annotation { "Feature Type Name" : "Feature", "Feature Type Description" : "" }
export const myFeature = defineFeature(function(context is Context, id is Id, definition is map)
    precondition{}
    {
        {
            var Q0;
            Q0=qCreatedBy(makeId("Front.planeOp"),FACE);
            var sketch = newSketch(context, id + "F0", { "sketchPlane" : qUnion([Q0])});
            skLineSegment(sketch, "E0.bottom", {"start": v(-23.42, 52.83) * mm, "end": v(52.78, 52.83) * mm});
            skLineSegment(sketch, "E0.top", {"start": v(-23.42, -61.47) * mm, "end": v(52.78, -61.47) * mm});
            skLineSegment(sketch, "E0.left", {"start": v(-23.42, 52.83) * mm, "end": v(-23.42, -61.47) * mm});
            skLineSegment(sketch, "E0.right", {"start": v(52.78, 52.83) * mm, "end": v(52.78, -61.47) * mm});
            skSolve(sketch);
        }
        {
            var Q0;
            Q0 = qSketchRegion(id + "F0", true);
            extrude(context, id + "F1", {"entities" : qUnion([Q0]), "depth" : 3.17 * mm});
        }
        {
            var Q0;
            Q0=makeQuery(id+"F1.opExtrude","CAP_FACE",FACE,{"disambiguationData":[OSD([sQuery(id+"F0.wireOp",EDGE,"E0.bottom"),sQuery(id+"F0.wireOp",EDGE,"E0.top"),sQuery(id+"F0.wireOp",EDGE,"E0.left"),sQuery(id+"F0.wireOp",EDGE,"E0.right")])],"isStart":false});
            var sketch = newSketch(context, id + "F2", { "sketchPlane" : qUnion([Q0])});
            skText(sketch, "E1", { "text": "STEM Academy\n", "fontName": "OpenSans-Regular.ttf"});
            const initialGuessF2  = {"E1": [-0.02342, 0.0339, 1, 0, 0.00766]};
            skSetInitialGuess(sketch, initialGuessF2);
            skSolve(sketch);
        }
        {
            var Q0;
            Q0 = qSketchRegion(id + "F2", true);
            extrude(context, id + "F3", {"entities" : qUnion([Q0]), "operationType" : NewBodyOperationType.REMOVE, "oppositeDirection" : true, "depth" : 3.17 * mm});
        }
        {
            var Q0;
            {var subQ0=sQuery(id+"F0.wireOp",EDGE,"E0.top");var subQ1=sQuery(id+"F0.wireOp",EDGE,"E0.right");var subQ2=sQuery(id+"F0.wireOp",EDGE,"E0.bottom");var subQ3=sQuery(id+"F0.wireOp",EDGE,"E0.left");Q0=makeQuery(id+"F3.boolean.opBoolean","SPLIT",FACE,{"disambiguationData":[TD([makeQuery(id+"F1.opExtrude","SWEPT_FACE",FACE,{"disambiguationData":[OSD([subQ2])]})])],"derivedFrom":makeQuery(id+"F1.opExtrude","CAP_FACE",FACE,{"disambiguationData":[OSD([subQ2,subQ0,subQ3,subQ1])],"isStart":false})});}
            var sketch = newSketch(context, id + "F4", { "sketchPlane" : qUnion([Q0])});
            skCircle(sketch, "E2", {"center": v(12.38, 47.2) * mm, "radius": 3.66 * mm});
            skSolve(sketch);
        }
        {
            var Q0;
            Q0 = qSketchRegion(id + "F4", true);
            extrude(context, id + "F5", {"entities" : qUnion([Q0]), "operationType" : NewBodyOperationType.REMOVE, "oppositeDirection" : true, "depth" : 25.4 * mm});
        }
        {
            var Q0;
            {var subQ0=sQuery(id+"F0.wireOp",EDGE,"E0.top");var subQ1=sQuery(id+"F0.wireOp",EDGE,"E0.right");var subQ2=sQuery(id+"F0.wireOp",EDGE,"E0.bottom");var subQ3=sQuery(id+"F0.wireOp",EDGE,"E0.left");Q0=makeQuery(id+"F3.boolean.opBoolean","SPLIT",FACE,{"disambiguationData":[TD([makeQuery(id+"F1.opExtrude","SWEPT_FACE",FACE,{"disambiguationData":[OSD([subQ2])]})])],"derivedFrom":makeQuery(id+"F1.opExtrude","CAP_FACE",FACE,{"disambiguationData":[OSD([subQ2,subQ0,subQ3,subQ1])],"isStart":false})});}
            var sketch = newSketch(context, id + "F6", { "sketchPlane" : qUnion([Q0])});
            skLineSegment(sketch, "E3", {"start": v(11.92, 3.65) * mm, "end": v(20.18, 18.93) * mm});
            skLineSegment(sketch, "E4", {"start": v(20.18, 18.93) * mm, "end": v(22.17, 21.21) * mm});
            skLineSegment(sketch, "E5", {"start": v(22.17, 21.21) * mm, "end": v(28.2, 12.78) * mm});
            skLineSegment(sketch, "E6", {"start": v(28.2, 12.78) * mm, "end": v(31.1, 12.78) * mm});
            skLineSegment(sketch, "E7", {"start": v(31.1, 12.78) * mm, "end": v(26.51, 3.38) * mm});
            skLineSegment(sketch, "E8", {"start": v(26.51, 3.38) * mm, "end": v(15.18, 3.38) * mm});
            skLineSegment(sketch, "E9", {"start": v(15.18, 3.38) * mm, "end": v(17.03, 6.8) * mm});
            skLineSegment(sketch, "E10", {"start": v(17.03, 6.8) * mm, "end": v(14.39, 8.22) * mm});
            skLineSegment(sketch, "E11", {"start": v(6.33, 21.79) * mm, "end": v(22.17, 21.21) * mm});
            skLineSegment(sketch, "E12", {"start": v(9.64, -3.37) * mm, "end": v(7.37, -2.15) * mm});
            skLineSegment(sketch, "E13", {"start": v(11.92, -6.2) * mm, "end": v(11.92, -20.73) * mm});
            skLineSegment(sketch, "E14", {"start": v(11.92, -20.73) * mm, "end": v(0, -20.73) * mm});
            skPoint(sketch, "E15.endSnap0", {"position": v(11.92, -13.46) * mm});
            skPoint(sketch, "E15.endSnap1", {"position": v(-3.98, -13.02) * mm});
            skLineSegment(sketch, "E16", {"start": v(19.76, -24.27) * mm, "end": v(19.76, -20.73) * mm});
            skLineSegment(sketch, "E17", {"start": v(19.76, -20.73) * mm, "end": v(30.37, -18.8) * mm});
            skLineSegment(sketch, "E18", {"start": v(30.37, -18.8) * mm, "end": v(38.07, -4.56) * mm});
            skLineSegment(sketch, "E19", {"start": v(38.07, -4.56) * mm, "end": v(32.73, 5.78) * mm});
            skLineSegment(sketch, "E20", {"start": v(32.73, 5.78) * mm, "end": v(21.53, 0) * mm});
            skLineSegment(sketch, "E21", {"start": v(21.53, 0) * mm, "end": v(30.81, -17.98) * mm});
            skLineSegment(sketch, "E22", {"start": v(19.76, -4.34) * mm, "end": v(19.76, -8.99) * mm});
            skPoint(sketch, "E22.endSnap0", {"position": v(26.17, -8.99) * mm});
            skLineSegment(sketch, "E23", {"start": v(19.76, -8.99) * mm, "end": v(26.17, -8.99) * mm});
            skLineSegment(sketch, "E24", {"start": v(11.92, 3.65) * mm, "end": v(0, 10.1) * mm});
            skLineSegment(sketch, "E25", {"start": v(0, 10.1) * mm, "end": v(6.33, 21.79) * mm});
            skLineSegment(sketch, "E26", {"start": v(0, -20.73) * mm, "end": v(-8.22, -5.67) * mm});
            skLineSegment(sketch, "E27", {"start": v(-8.22, -5.67) * mm, "end": v(-3.98, 3.58) * mm});
            skLineSegment(sketch, "E28", {"start": v(-3.98, 3.58) * mm, "end": v(-7.03, 4.98) * mm});
            skLineSegment(sketch, "E29", {"start": v(-7.03, 4.98) * mm, "end": v(3.38, 6.48) * mm});
            skLineSegment(sketch, "E30", {"start": v(3.38, 6.48) * mm, "end": v(9.64, -3.37) * mm});
            skLineSegment(sketch, "E31", {"start": v(11.92, -6.2) * mm, "end": v(5.2, -6.2) * mm});
            skLineSegment(sketch, "E32", {"start": v(5.2, -6.2) * mm, "end": v(7.37, -2.15) * mm});
            skLineSegment(sketch, "E33", {"start": v(19.76, -24.27) * mm, "end": v(13.36, -13.1) * mm});
            skLineSegment(sketch, "E34", {"start": v(13.36, -13.1) * mm, "end": v(19.76, -4.34) * mm});
            skSolve(sketch);
        }
        {
            var Q0;
            Q0=makeQuery(id+"F6.imprint","IMPRINT",FACE,{"disambiguationData":[TD([[makeQuery(id+"F6.imprint","IMPRINT",EDGE,{"derivedFrom":sQuery(id+"F6.wireOp",EDGE,"E5")}),1.0]])]});
            var sketch = newSketch(context, id + "F7", { "sketchPlane" : qUnion([Q0])});
            skText(sketch, "E35", { "text": "Hall Pass\n", "fontName": "OpenSans-Regular.ttf"});
            const initialGuessF7  = {"E35": [-0.01784, -0.05735, 1, 0, 0.0113]};
            skSetInitialGuess(sketch, initialGuessF7);
            skSolve(sketch);
        }
        {
            var Q0;
            Q0 = qSketchRegion(id + "F7", true);
            extrude(context, id + "F8", {"entities" : qUnion([Q0]), "operationType" : NewBodyOperationType.REMOVE, "oppositeDirection" : true, "depth" : 1 / 203.2 * mm});
        }
        {
            var Q0;
            Q0 = qSketchRegion(id + "F6", true);
            extrude(context, id + "F9", {"entities" : qUnion([Q0]), "operationType" : NewBodyOperationType.REMOVE, "oppositeDirection" : true, "depth" : 3.17 * mm});
        }
    });